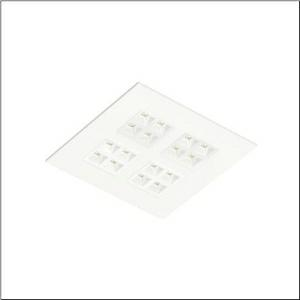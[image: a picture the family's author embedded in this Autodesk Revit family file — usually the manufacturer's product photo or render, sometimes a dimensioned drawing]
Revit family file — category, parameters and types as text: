
# Revit family: silica_r__31_square_51my6nms34wa_c159
name_source: partatom
category: Lighting Fixtures
units: mm (PartAtom-declared; Revit-internal decimal feet)

## family parameters
Cut with Voids When Loaded = No
Host = Face
Light Source = No
Part Type = Normal
Room Calculation Point = No
Round Connector Dimension = Use Diameter
Shared = No

## types (1)
- --- (1 x LED, 6600 lm, 39 W, 3000K)
    Apparent Load = 39 VA
    CIE Flux Codes = 81 99 100 100 100
    Color Rendering = 80
    Color Temperature = 3000K
    Default Elevation = 1800 mm
    Description = Silica® 31 Square, office luminaire, primary light control with lens, of PMMA, primary anti-glare with reflector, of PC, white, light emission: direct distribution, primary light characteristic: symmetric, installation type: lay-in mounting, LED, rated luminous flux: 4.580lm, luminous efficacy: 176lm/W, light colour: 830, colour temperature: 3000K, control gear: ON/OFF Multilumen, with terminal, 3-pole, mains connection: 220..240V, AC, 50/60Hz, rated input power: 26W, luminaire housing, of sheet steel, coated, traffic white (RAL 9016), module: M600, length: 595mm, width: 595mm, height: 43mm, protection rating (complete): IP20, insulation class (complete): insulation class II (safety insulation), certification: CE, impact resistance: IK03, permissible operating ambient temperature: -20..+35°C, standard: EN 50419, packaging unit: 1 piece
    Height = 0 mm  [stored 0 ft]
    Lamp = 1 x LED
    Lamp Light Flux = 6600 lm
    Lamp Power = 39 W
    Lamp count = 1
    Length = 595 mm
    Luminous efficacy = 169 lm/W
    Manufacturer = Siteco
    ModVariant = No
    Model = 51MY6NMS34WA
    Mounting Place = Ceiling
    Mounting Type = Recessed
    Number of Poles = 1
    OnlyDefault = Yes
    Power Factor = 1
    Product Name = Silica® 31 Square
    Product group = office luminaire | ceiling recessed
    ProductGroupID = 400
    Protection Class = Protection class II
    Protection Degree = IP 20
    RLX_Detail_Level = 1
    RLX_Emergency_Light_Flux = 0 lm
    RLX_Emergency_Type = 0
    RLX_Emergency_Type_DB = No
    RlxData = <blob elided: 28801 chars, md5=03924c2c>
    Socket = socket
    Standby Power = 0 W
    System Light Flux = 6600 lm
    System Power = 39 W
    Type Comments = factory setting: luminous flux: 100 % | (ON | ON | ON | ON) | 1100 mA
    Type Image = l_1313651.jpg
    URL = http://relux.com
    VarID = @adj_056417
    Voltage = 0 V
    Weight = 0.00 kg
    Width = 595 mm

note: [stored X ft] marks values corroborated as IEEE doubles in the binary element streams (Revit-internal decimal feet)

## geometry (parser evidence)
native form markers: Blend x4, Sweep x8
no freeform markers — native parametric forms only
